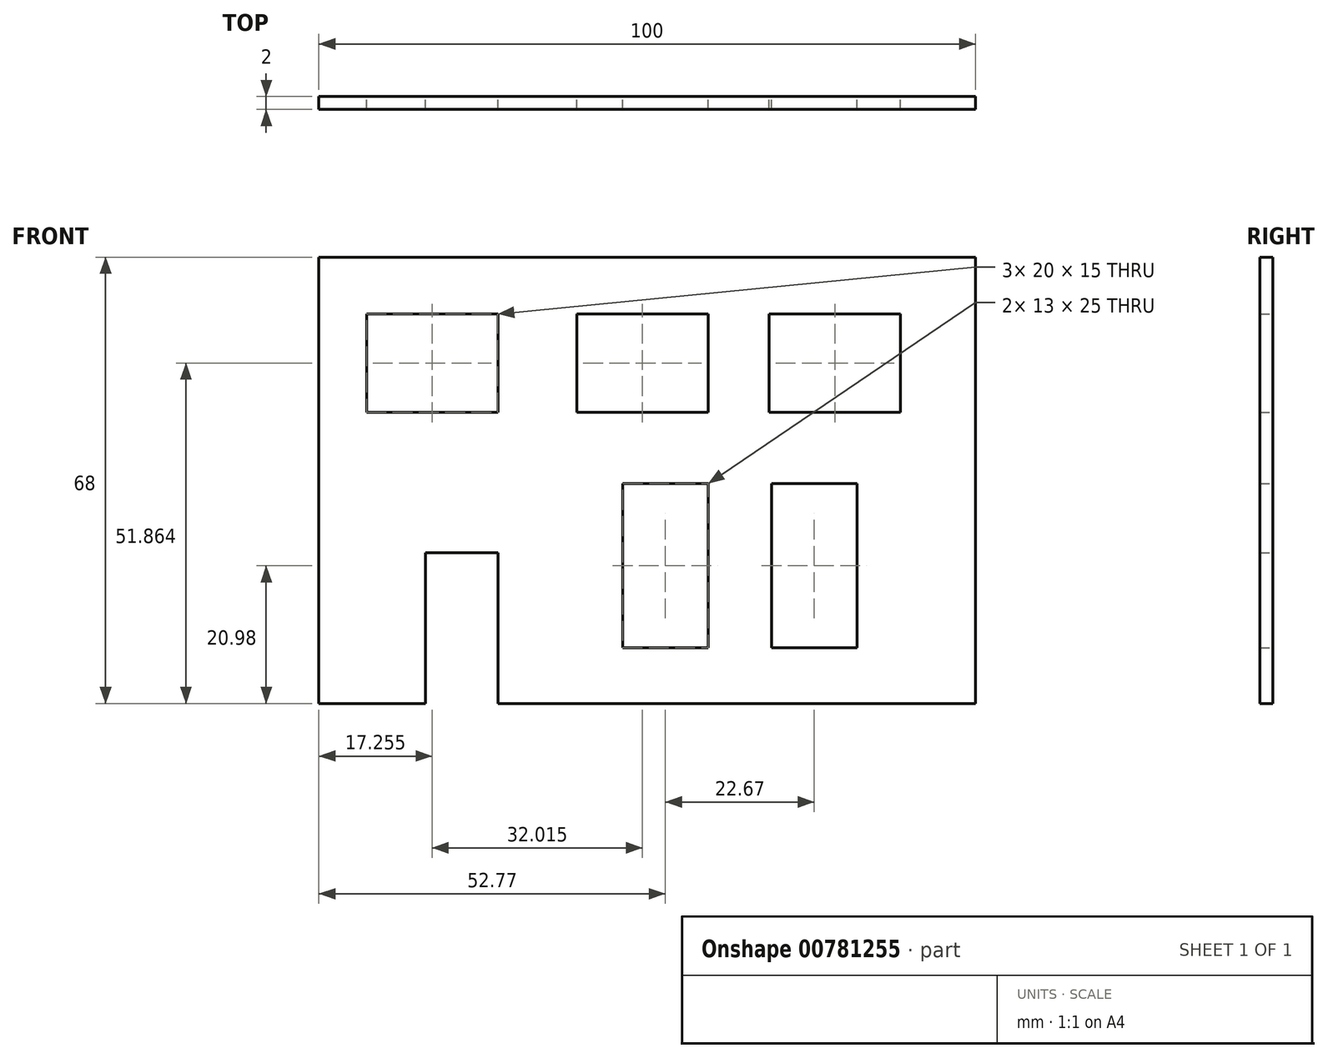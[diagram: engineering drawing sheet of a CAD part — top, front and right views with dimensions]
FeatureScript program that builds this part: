
annotation { "Feature Type Name" : "Feature", "Feature Type Description" : "" }
export const myFeature = defineFeature(function(context is Context, id is Id, definition is map)
    precondition{}
    {
        {
            var Q0;
            Q0=qCreatedBy(makeId("Front.planeOp"),FACE);
            var sketch = newSketch(context, id + "F0", { "sketchPlane" : qUnion([Q0])});
            skLineSegment(sketch, "E0.bottom", {"start": v(-59.72, 34.52) * mm, "end": v(40.28, 34.52) * mm});
            skLineSegment(sketch, "E0.top", {"start": v(-59.72, -33.48) * mm, "end": v(40.28, -33.48) * mm});
            skLineSegment(sketch, "E0.left", {"start": v(-59.72, 34.52) * mm, "end": v(-59.72, -33.48) * mm});
            skLineSegment(sketch, "E0.right", {"start": v(40.28, 34.52) * mm, "end": v(40.28, -33.48) * mm});
            skLineSegment(sketch, "E1", {"start": v(-59.72, -33.48) * mm, "end": v(-43.47, -33.48) * mm});
            skLineSegment(sketch, "E2.bottom", {"start": v(-43.47, -33.48) * mm, "end": v(-32.47, -33.48) * mm});
            skLineSegment(sketch, "E2.top", {"start": v(-43.47, -10.48) * mm, "end": v(-32.47, -10.48) * mm});
            skLineSegment(sketch, "E2.left", {"start": v(-43.47, -33.48) * mm, "end": v(-43.47, -10.48) * mm});
            skLineSegment(sketch, "E2.right", {"start": v(-32.47, -33.48) * mm, "end": v(-32.47, -10.48) * mm});
            skLineSegment(sketch, "E3.bottom", {"start": v(-52.47, 25.88) * mm, "end": v(-32.47, 25.88) * mm});
            skLineSegment(sketch, "E3.top", {"start": v(-52.47, 10.88) * mm, "end": v(-32.47, 10.88) * mm});
            skLineSegment(sketch, "E3.left", {"start": v(-52.47, 25.88) * mm, "end": v(-52.47, 10.88) * mm});
            skLineSegment(sketch, "E3.right", {"start": v(-32.47, 25.88) * mm, "end": v(-32.47, 10.88) * mm});
            skLineSegment(sketch, "E4.bottom", {"start": v(-13.45, 0) * mm, "end": v(-0.45, 0) * mm});
            skLineSegment(sketch, "E4.top", {"start": v(-13.45, -25) * mm, "end": v(-0.45, -25) * mm});
            skLineSegment(sketch, "E4.left", {"start": v(-13.45, 0) * mm, "end": v(-13.45, -25) * mm});
            skLineSegment(sketch, "E4.right", {"start": v(-0.45, 0) * mm, "end": v(-0.45, -25) * mm});
            skLineSegment(sketch, "E5.bottom", {"start": v(9.22, 0) * mm, "end": v(22.22, 0) * mm});
            skLineSegment(sketch, "E5.top", {"start": v(9.22, -25) * mm, "end": v(22.22, -25) * mm});
            skLineSegment(sketch, "E5.left", {"start": v(9.22, 0) * mm, "end": v(9.22, -25) * mm});
            skLineSegment(sketch, "E5.right", {"start": v(22.22, 0) * mm, "end": v(22.22, -25) * mm});
            skLineSegment(sketch, "E6.bottom", {"start": v(-20.45, 25.88) * mm, "end": v(-0.45, 25.88) * mm});
            skLineSegment(sketch, "E6.top", {"start": v(-20.45, 10.88) * mm, "end": v(-0.45, 10.88) * mm});
            skLineSegment(sketch, "E6.left", {"start": v(-20.45, 25.88) * mm, "end": v(-20.45, 10.88) * mm});
            skLineSegment(sketch, "E6.right", {"start": v(-0.45, 25.88) * mm, "end": v(-0.45, 10.88) * mm});
            skLineSegment(sketch, "E7.bottom", {"start": v(8.87, 25.88) * mm, "end": v(28.87, 25.88) * mm});
            skLineSegment(sketch, "E7.top", {"start": v(8.87, 10.88) * mm, "end": v(28.87, 10.88) * mm});
            skLineSegment(sketch, "E7.left", {"start": v(8.87, 25.88) * mm, "end": v(8.87, 10.88) * mm});
            skLineSegment(sketch, "E7.right", {"start": v(28.87, 25.88) * mm, "end": v(28.87, 10.88) * mm});
            skSolve(sketch);
        }
        {
            var Q0;
            Q0=makeQuery(id+"F0.imprint","IMPRINT",FACE,{"disambiguationData":[TD([[makeQuery(id+"F0.imprint","IMPRINT",EDGE,{"derivedFrom":sQuery(id+"F0.wireOp",EDGE,"E0.bottom")}),-1.0]])]});
            extrude(context, id + "F1", {"entities" : qUnion([Q0]), "depth" : 2 * mm, "offsetDistance" : 25 * mm});
        }
    });
